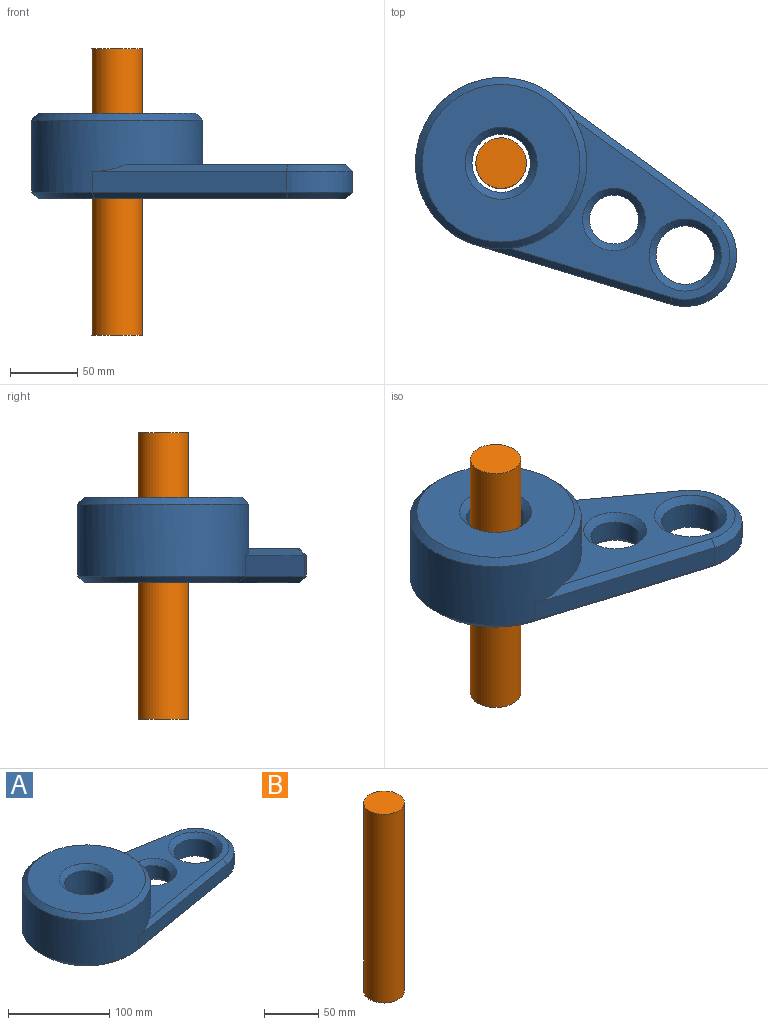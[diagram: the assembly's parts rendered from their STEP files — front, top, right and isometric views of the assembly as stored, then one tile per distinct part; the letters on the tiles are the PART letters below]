
ASSEMBLY  parts=2 mates=1
PART A: 23 faces, bbox 254x127x63.5 mm
  f0: cylinder r=38.1mm len=75.13mm, axis (0,0,-1), area 1629.7mm2, adj f1,f3,f11,f16
  f1: plane 148.17x25.04mm, normal (0.17,0.99,0), area 2290.1mm2, adj f0,f2,f12,f17
  f2: cylinder r=63.5mm len=127mm, axis (0,0,-1), area 17832.9mm2, adj f1,f3,f6,f10,f14,f15,f17
  f3: plane 148.17x25.04mm, normal (0.17,-0.99,0), area 2290.1mm2, adj f0,f2,f9,f15
  f4: cylinder r=21.63mm len=43.26mm, axis (0,0,-1), area 2761.6mm2, adj f7,f18
  f5: cylinder r=21.63mm len=53.34mm, axis (0,0,-1), area 7249.2mm2, adj f13,f19
  f6: plane 151.14x106.91mm, normal (0,0,1), area 5846.8mm2, adj f2,f15,f16,f17,f18,f22
  f7: plane 243.84x116.84mm, normal (0,0,-1), area 15798.1mm2, adj f4,f9,f10,f11,f12,f13,f21
  f8: plane 116.84x116.84mm, normal (0,0,1), area 8480.7mm2, adj f14,f19
  f9: plane 149.01x30.05mm, normal (0.12,-0.7,-0.71), area 1079.6mm2, adj f3,f7,f10,f11
  f10: cone r=63.5mm half-angle=45deg, axis (0,0,1), area 1522.5mm2, adj f2,f7,f9,f12
  f11: cone r=38.1mm half-angle=45deg, axis (0,0,1), area 717mm2, adj f0,f7,f9,f12
  f12: plane 149.01x30.05mm, normal (0.12,0.7,-0.71), area 1079.6mm2, adj f1,f7,f10,f11
  f13: cone r=26.71mm half-angle=45deg, axis (0,0,-1), area 1091mm2, adj f5,f7
  f14: cone r=58.42mm half-angle=45deg, axis (0,0,-1), area 2751.7mm2, adj f2,f8
  f15: plane 148.17x30.05mm, normal (0.12,-0.7,0.71), area 959.4mm2, adj f2,f3,f6,f16
  f16: cone r=33.02mm half-angle=45deg, axis (0,0,-1), area 717mm2, adj f0,f6,f15,f17
  f17: plane 148.17x30.05mm, normal (0.12,0.7,0.71), area 959.4mm2, adj f1,f2,f6,f16
  f18: cone r=21.63mm half-angle=45deg, axis (0,0,1), area 1091mm2, adj f4,f6
  f19: cone r=21.63mm half-angle=45deg, axis (0,0,1), area 1091mm2, adj f5,f8
  f20: cylinder r=18.14mm len=36.28mm, axis (0,0,1), area 1737.1mm2, adj f21,f22
  f21: cone r=23.22mm half-angle=45deg, axis (0,0,-1), area 933.5mm2, adj f7,f20
  f22: cone r=18.14mm half-angle=45deg, axis (0,0,1), area 933.5mm2, adj f6,f20
PART B: 3 faces, bbox 37.4x37.4x212.3 mm
  f0: cylinder r=18.68mm len=212.25mm, axis (0,0,-1), area 24910.1mm2, adj f1,f2
  f1: plane 37.36x37.36mm, normal (0,0,1), area 1096.1mm2, adj f0
  f2: plane 37.36x37.36mm, normal (0,0,-1), area 1096.1mm2, adj f0
PLACE A rot(axis=(0,0,-1),26.5deg) t=(-74.96,-84.61,101.05)mm
PLACE B at identity fixed
MATE revolute A.f2 <-> B.f0  axis (0,0,-1) through (-74.96,-84.61,106.13)mm
